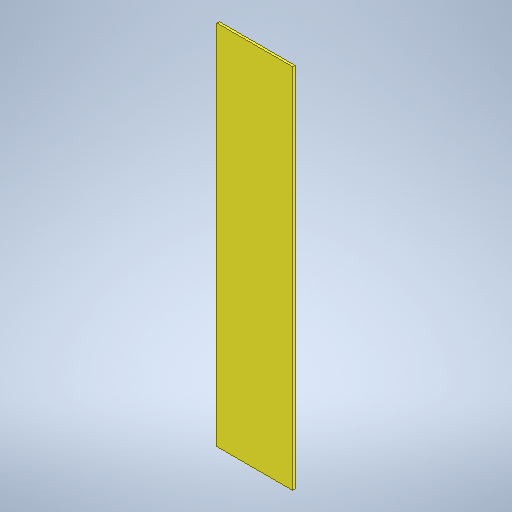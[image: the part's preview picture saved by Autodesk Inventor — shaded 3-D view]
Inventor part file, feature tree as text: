
AUTODESK INVENTOR PART (.ipt)
format: ipt  version: 2025.1 (Build 291241020, 241B)  size: 250,880 bytes
history: native  units: in
note: dims shown in document units (in); Inventor stores cm internally (conversion verified against a paired STEP export)
features: extrude x1, sketch x1
ambient origin geometry x8: Origin, YZ Plane, XZ Plane, XY Plane, X Axis, Y Axis, Z Axis, Center Point
bodies: Solid1 (feature_tree)
feature tree (2):
  extrude  "Extrusion1"  Depth=19.831in
  sketch  "Sketch1"  dims[d2=96.0in d3=19.831in d4=0.625in d5=0.0in]
